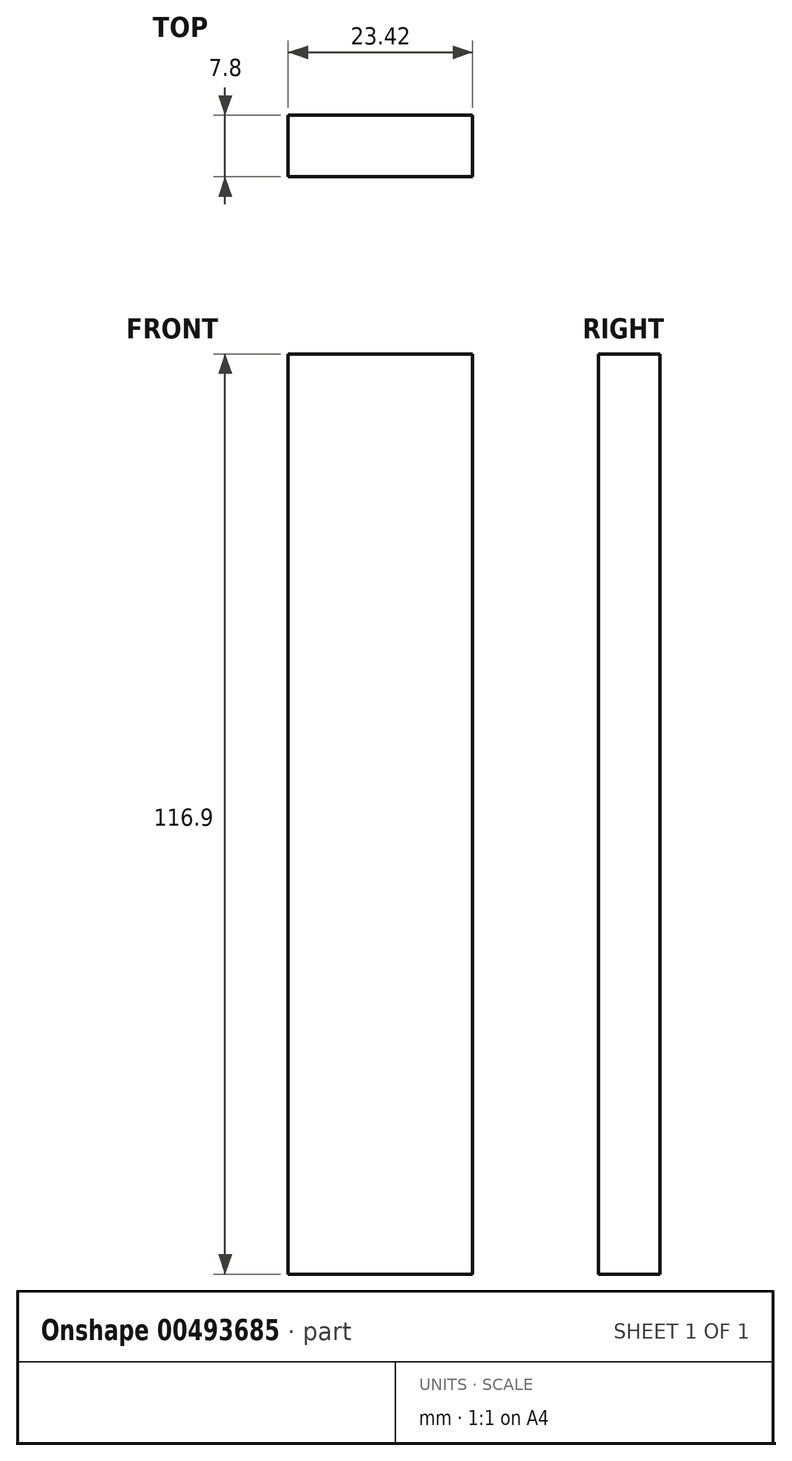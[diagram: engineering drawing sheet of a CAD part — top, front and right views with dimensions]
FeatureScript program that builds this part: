
annotation { "Feature Type Name" : "Feature", "Feature Type Description" : "" }
export const myFeature = defineFeature(function(context is Context, id is Id, definition is map)
    precondition{}
    {
        {
            var Q0;
            Q0=qCreatedBy(makeId("Front.planeOp"),FACE);
            var sketch = newSketch(context, id + "F0", { "sketchPlane" : qUnion([Q0])});
            skLineSegment(sketch, "E0.bottom", {"start": v(-11.7, 58.45) * mm, "end": v(11.7, 58.45) * mm});
            skLineSegment(sketch, "E0.top", {"start": v(-11.7, -58.45) * mm, "end": v(11.7, -58.45) * mm});
            skLineSegment(sketch, "E0.left", {"start": v(-11.7, 58.45) * mm, "end": v(-11.7, -58.45) * mm});
            skLineSegment(sketch, "E0.right", {"start": v(11.7, 58.45) * mm, "end": v(11.7, -58.45) * mm});
            skPoint(sketch, "E0.middle", {"position": v(0, 0) * mm});
            skSolve(sketch);
        }
        {
            var Q0;
            Q0=makeQuery(id+"F0.imprint","IMPRINT",FACE,{"disambiguationData":[TD([[makeQuery(id+"F0.imprint","IMPRINT",EDGE,{"derivedFrom":sQuery(id+"F0.wireOp",EDGE,"E0.bottom")}),-1.0]])]});
            extrude(context, id + "F1", {"entities" : qUnion([Q0]), "endBound" : BoundingType.SYMMETRIC, "depth" : 7.8 * mm});
        }
    });
